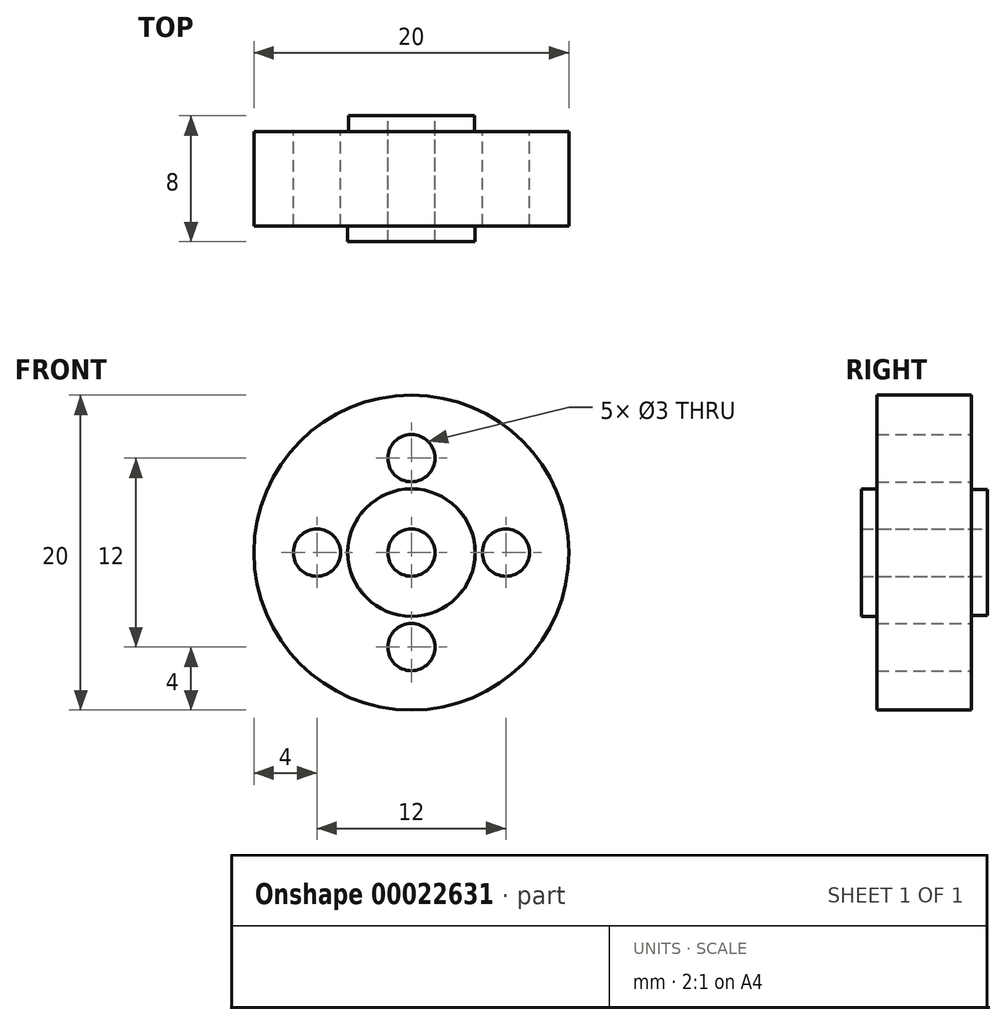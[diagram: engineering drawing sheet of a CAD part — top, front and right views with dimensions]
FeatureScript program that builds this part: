
annotation { "Feature Type Name" : "Feature", "Feature Type Description" : "" }
export const myFeature = defineFeature(function(context is Context, id is Id, definition is map)
    precondition{}
    {
        {
            var Q0;
            Q0=qCreatedBy(makeId("Front.planeOp"),FACE);
            var sketch = newSketch(context, id + "F0", { "sketchPlane" : qUnion([Q0])});
            skCircle(sketch, "E0", {"center": v(0, 0) * mm, "radius": 10 * mm});
            skCircle(sketch, "E1", {"center": v(0, 0) * mm, "radius": 4 * mm});
            skCircle(sketch, "E2", {"center": v(0, 6) * mm, "radius": 1.5 * mm});
            skCircle(sketch, "E3.1.0", {"center": v(-6, 0) * mm, "radius": 1.5 * mm});
            skCircle(sketch, "E3.2.0", {"center": v(0, -6) * mm, "radius": 1.5 * mm});
            skCircle(sketch, "E3.3.0", {"center": v(6, 0) * mm, "radius": 1.5 * mm});
            skSolve(sketch);
        }
        {
            var Q0;
            Q0=makeQuery(id+"F0.imprint","IMPRINT",FACE,{"disambiguationData":[TD([[makeQuery(id+"F0.imprint","IMPRINT",EDGE,{"derivedFrom":sQuery(id+"F0.wireOp",EDGE,"E0")}),1.0]])]});
            extrude(context, id + "F1", {"entities" : qUnion([Q0]), "endBound" : BoundingType.SYMMETRIC, "depth" : 6 * mm});
        }
        {
            var Q0;
            Q0=makeQuery(id+"F1.opExtrude","CAP_FACE",FACE,{"disambiguationData":[OSD([sQuery(id+"F0.wireOp",EDGE,"E0"),sQuery(id+"F0.wireOp",EDGE,"E1"),sQuery(id+"F0.wireOp",EDGE,"E2"),sQuery(id+"F0.wireOp",EDGE,"E3.1.0"),sQuery(id+"F0.wireOp",EDGE,"E3.2.0"),sQuery(id+"F0.wireOp",EDGE,"E3.3.0")])],"isStart":true});
            var sketch = newSketch(context, id + "F2", { "sketchPlane" : qUnion([Q0])});
            skCircle(sketch, "E4", {"center": v(0, 0) * mm, "radius": 4.05 * mm});
            skSolve(sketch);
        }
        {
            var Q0;
            Q0 = qSketchRegion(id + "F2", true);
            extrude(context, id + "F3", {"entities" : qUnion([Q0]), "operationType" : NewBodyOperationType.ADD, "oppositeDirection" : true, "depth" : 7 * mm});
        }
        {
            var Q0;
            Q0=makeQuery(id+"F3.boolean.opBoolean","MERGE",FACE,{"derivedFrom":[makeQuery(id+"F1.opExtrude","CAP_FACE",FACE,{"disambiguationData":[OSD([sQuery(id+"F0.wireOp",EDGE,"E0"),sQuery(id+"F0.wireOp",EDGE,"E1"),sQuery(id+"F0.wireOp",EDGE,"E2"),sQuery(id+"F0.wireOp",EDGE,"E3.1.0"),sQuery(id+"F0.wireOp",EDGE,"E3.2.0"),sQuery(id+"F0.wireOp",EDGE,"E3.3.0")])],"isStart":true}),makeQuery(id+"F3.opExtrude","CAP_FACE",FACE,{"disambiguationData":[OSD([sQuery(id+"F2.wireOp",EDGE,"E4")])],"isStart":true})]});
            var sketch = newSketch(context, id + "F4", { "sketchPlane" : qUnion([Q0])});
            skCircle(sketch, "E5", {"center": v(0, 0) * mm, "radius": 4 * mm});
            skSolve(sketch);
        }
        {
            var Q0;
            Q0 = qSketchRegion(id + "F4", true);
            extrude(context, id + "F5", {"entities" : qUnion([Q0]), "operationType" : NewBodyOperationType.ADD, "depth" : 1 * mm});
        }
        {
            var Q0;
            Q0=makeQuery(id+"F5.opExtrude","CAP_FACE",FACE,{"disambiguationData":[OSD([sQuery(id+"F4.wireOp",EDGE,"E5")])],"isStart":false});
            var sketch = newSketch(context, id + "F6", { "sketchPlane" : qUnion([Q0])});
            skCircle(sketch, "E6", {"center": v(0, 0) * mm, "radius": 1.5 * mm});
            skSolve(sketch);
        }
        {
            var Q0;
            Q0=makeQuery(id+"F6.imprint","IMPRINT",FACE,{"disambiguationData":[TD([[makeQuery(id+"F6.imprint","IMPRINT",EDGE,{"derivedFrom":sQuery(id+"F6.wireOp",EDGE,"E6")}),1.0]])]});
            var Q1;
            Q1=sQuery(id+"F6.wireOp",EDGE,"E6");
            extrude(context, id + "F7", {"entities" : qUnion([Q0]), "operationType" : NewBodyOperationType.REMOVE, "surfaceEntities" : qUnion([Q1]), "oppositeDirection" : true, "depth" : 25.4 * mm});
        }
    });
